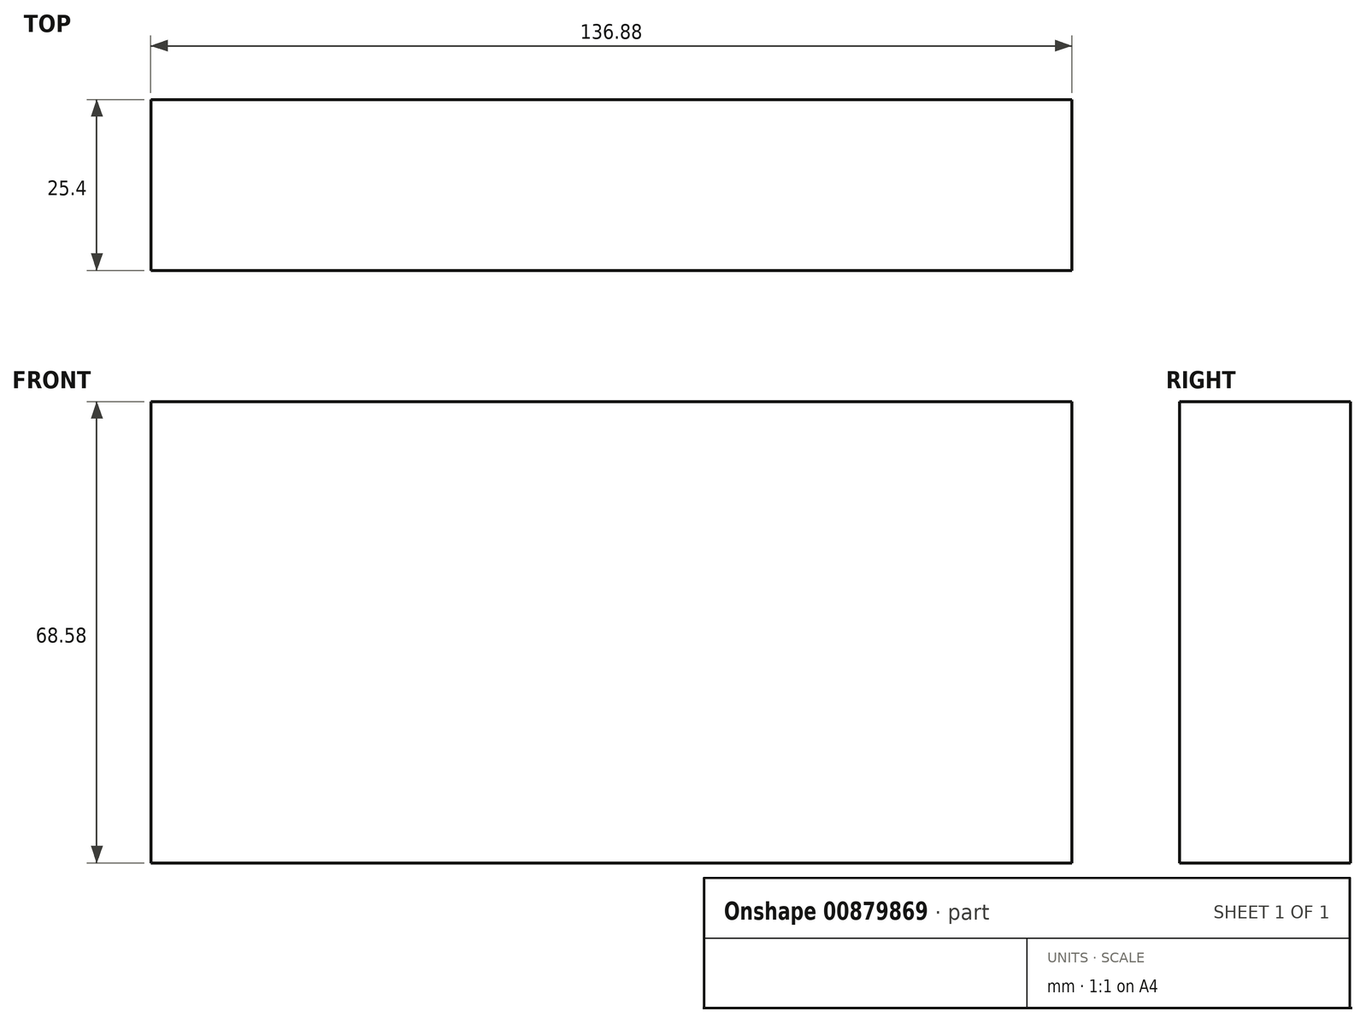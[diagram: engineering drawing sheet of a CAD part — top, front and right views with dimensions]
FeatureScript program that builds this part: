
annotation { "Feature Type Name" : "Feature", "Feature Type Description" : "" }
export const myFeature = defineFeature(function(context is Context, id is Id, definition is map)
    precondition{}
    {
        {
            var Q0;
            Q0=qCreatedBy(makeId("Front.planeOp"),FACE);
            var sketch = newSketch(context, id + "F0", { "sketchPlane" : qUnion([Q0])});
            skLineSegment(sketch, "E0", {"start": v(-67.43, 55.18) * mm, "end": v(69.45, 55.18) * mm});
            skLineSegment(sketch, "E1", {"start": v(69.45, 55.18) * mm, "end": v(69.45, -13.4) * mm});
            skLineSegment(sketch, "E2", {"start": v(69.45, -13.4) * mm, "end": v(-67.43, -13.4) * mm});
            skLineSegment(sketch, "E3", {"start": v(-67.43, -13.4) * mm, "end": v(-67.43, 55.18) * mm});
            skSolve(sketch);
        }
        {
            var Q0;
            Q0 = qSketchRegion(id + "F0", true);
            extrude(context, id + "F1", {"entities" : qUnion([Q0]), "depth" : 25.4 * mm, "offsetDistance" : 25.4 * mm});
        }
    });
